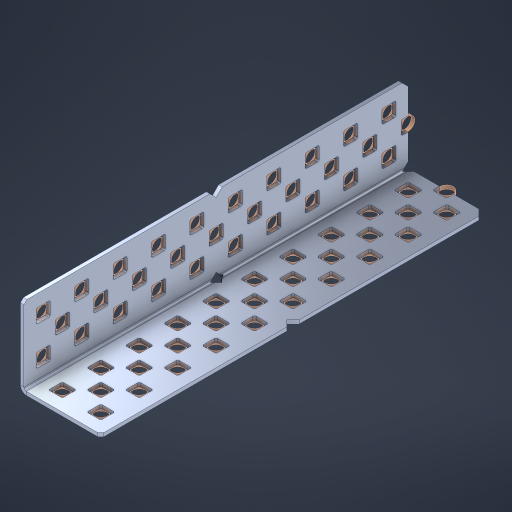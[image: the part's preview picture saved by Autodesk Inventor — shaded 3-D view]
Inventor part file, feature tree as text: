
AUTODESK INVENTOR PART (.ipt)
format: ipt  version: 2023 (Build 270158000, 158)  size: 969,216 bytes
history: native  units: in
note: dims shown in document units (in); Inventor stores cm internally (conversion verified against a paired STEP export)
features: other x66, extrude x58, sheet_metal_op x8, sketch x7, pattern_linear x2, mirror x1, chamfer x1
ambient origin geometry x8: Origin, YZ Plane, XZ Plane, XY Plane, X Axis, Y Axis, Z Axis, Center Point
bodies: Solid1 (feature_tree), Body (feature_tree)
feature tree (143):
  sheet_metal_op  "Flanges"
  sheet_metal_op  "Body Pattern"
  pattern_linear  "Center Pattern"  Spacing1=1.0in  [1 undecoded]
  other  "Arc Length"
  pattern_linear  "Notch Pattern"  Spacing1=0.1875in  [1 undecoded]
  other  "Diagonal Plane"
  mirror  "Everything Mirrored"
  chamfer  "End Chamfer"
  sketch  "Sketch1"  dims[d0=1.0in]
  other  "Plate1"
  sketch  "Sketch2"  dims[d1=5.0in]
  other  "Plate2"
  sheet_metal_op  "Bend1"
  sheet_metal_op  "Corner1"
  sketch  "Sketch8"  dims[d2=0.0469in]
  sketch  "Sketch9"  dims[d3=0.0469in]
  other  "Srf91"
  sheet_metal_op  "Body Pattern Sketch"
  other  "Srf92"
  sketch  "Sketch13"  dims[d4=0.0234in]
  sketch  "Sketch15"  dims[d5=0.0938in]
  sketch  "Sketch16"  dims[d6=0.0469in d7=1.0in d8=90.0deg d9=0.0312in d10=0.1875in d11=0.0469in d12=0.0469in d49=0.182in d50=0.02in d52=0.25in d53=0.0469in d54=0.0in d55=0.172in d56=1.0in d57=0.0in d60=3.937in d62=0.5in d63=0.7874in d65=0.5in d85=0.1473in d86=0.1659in d89=0.0469in d90=0.0in d91=0.04in d92=0.0491in d95=2.5in d96=0.04in d97=0.25in d98=45.0deg d99=0.25in d106=0.182in d107=0.02in d108=0.5in d110=0.0469in d111=0.0in d112=0.172in d113=0.5in d114=0.0in d117=0.5in d123=0.25in d125=0.25in d126=0.0491in d127=0.1227in d128=0.08in d129=0.04in d130=2.5in]
  other  "Srf786"
  other  "Srf856"
  other  "Srf857"
  other  "Srf858"
  other  "Srf859"
  other  "Srf860"
  other  "Srf861"
  other  "Srf889"
  other  "Srf890"
  other  "Srf891"
  other  "Srf1275"
  other  "Srf1276"
  other  "Srf1278"
  other  "Srf1279"
  other  "Srf1280"
  other  "Srf1281"
  other  "Srf1282"
  other  "Srf1283"
  other  "Srf1277"
  other  "Srf1285"
  other  "Srf1286"
  other  "Srf1287"
  other  "Srf1383"
  other  "Srf1384"
  other  "Srf1385"
  other  "Srf1386"
  other  "Srf1387"
  other  "Srf1388"
  other  "Srf1389"
  other  "Srf1390"
  other  "Srf1391"
  other  "Srf1392"
  other  "Srf1393"
  other  "Srf1394"
  other  "Srf1445"
  other  "Srf1446"
  other  "Srf1447"
  other  "Srf1448"
  other  "Srf1449"
  other  "Srf1450"
  other  "Srf1475"
  other  "Srf1476"
  other  "Srf1477"
  other  "Srf1478"
  other  "Srf1479"
  other  "Srf1480"
  other  "Srf1481"
  other  "Srf1482"
  other  "Srf1483"
  other  "Srf1484"
  other  "Srf1485"
  other  "Srf1486"
  other  "Srf1537"
  other  "Srf1538"
  other  "Srf1539"
  other  "Srf1540"
  other  "Srf1541"
  other  "Srf1542"
  sheet_metal_op  "Body Stamp"
  sheet_metal_op  "Body Circle"
  other  "Center Stamp"
  other  "Center Circle"
  sheet_metal_op  "Notch"
  extrude  "ExtrusionSrf92"  Depth=0.0469in
  extrude  "ExtrusionSrf856"  Depth=0.0469in
  extrude  "ExtrusionSrf857"  Depth=2.5in
  extrude  "ExtrusionSrf858"  Depth=0.02in
  extrude  "ExtrusionSrf859"  Depth=2.5in
  extrude  "ExtrusionSrf860"  Depth=0.0469in
  extrude  "ExtrusionSrf861"  TaperAngle=0.0deg  [1 undecoded]
  extrude  "ExtrusionSrf889"  Depth=2.5in
  extrude  "ExtrusionSrf890"  Depth=1.0in TaperAngle=0.0deg
  extrude  "ExtrusionSrf891"  Depth=2.5in
  extrude  "ExtrusionSrf1275"  Depth=0.5in
  extrude  "ExtrusionSrf1276"  Depth=2.5in
  extrude  "ExtrusionSrf1277"  Depth=2.5in
  extrude  "ExtrusionSrf1278"  Depth=0.0469in
  extrude  "ExtrusionSrf1279"  Depth=2.5in TaperAngle=0.0deg
  extrude  "ExtrusionSrf1280"  Depth=2.5in
  extrude  "ExtrusionSrf1281"  Depth=2.5in TaperAngle=45.0deg
  extrude  "ExtrusionSrf1282"  Depth=2.5in
  extrude  "ExtrusionSrf1345"  Depth=2.5in
  extrude  "ExtrusionSrf1346"  Depth=0.02in
  extrude  "ExtrusionSrf1347"  Depth=0.5in
  extrude  "ExtrusionSrf1348"  Depth=0.0469in
  extrude  "ExtrusionSrf1383"  TaperAngle=0.0deg  [1 undecoded]
  extrude  "ExtrusionSrf1384"  Depth=2.5in
  extrude  "ExtrusionSrf1385"  Depth=0.5in TaperAngle=0.0deg
  extrude  "ExtrusionSrf1386"  Depth=0.5in
  extrude  "ExtrusionSrf1387"  Depth=2.5in
  extrude  "ExtrusionSrf1388"  Depth=2.5in
  extrude  "ExtrusionSrf1389"  Depth=2.5in
  extrude  "ExtrusionSrf1390"  Depth=2.5in
  extrude  "ExtrusionSrf1391"  Depth=2.5in
  extrude  "ExtrusionSrf1392"  Depth=2.5in
  extrude  "ExtrusionSrf1393"  Depth=2.5in
  extrude  "ExtrusionSrf1394"  [1 undecoded]
  extrude  "ExtrusionSrf1445"  [1 undecoded]
  extrude  "ExtrusionSrf1446"  [1 undecoded]
  extrude  "ExtrusionSrf1447"  [1 undecoded]
  extrude  "ExtrusionSrf1448"  [1 undecoded]
  extrude  "ExtrusionSrf1449"  [1 undecoded]
  extrude  "ExtrusionSrf1450"  [1 undecoded]
  extrude  "ExtrusionSrf1475"  [1 undecoded]
  extrude  "ExtrusionSrf1476"  [1 undecoded]
  extrude  "ExtrusionSrf1477"  [1 undecoded]
  extrude  "ExtrusionSrf1478"  [1 undecoded]
  extrude  "ExtrusionSrf1479"  [1 undecoded]
  extrude  "ExtrusionSrf1480"  [1 undecoded]
  extrude  "ExtrusionSrf1481"  [1 undecoded]
  extrude  "ExtrusionSrf1482"  [1 undecoded]
  extrude  "ExtrusionSrf1483"  [1 undecoded]
  extrude  "ExtrusionSrf1484"  [1 undecoded]
  extrude  "ExtrusionSrf1485"  [1 undecoded]
  extrude  "ExtrusionSrf1486"  [1 undecoded]
  extrude  "ExtrusionSrf1537"  [1 undecoded]
  extrude  "ExtrusionSrf1538"  [1 undecoded]
  extrude  "ExtrusionSrf1539"  [1 undecoded]
  extrude  "ExtrusionSrf1540"  [1 undecoded]
  extrude  "ExtrusionSrf1541"  [1 undecoded]
  extrude  "ExtrusionSrf1542"  [1 undecoded]
note: 29 required parameter values undecoded (feature->parameter linkage not recoverable at this tier; creation-order binding heuristic only, values carry confidence <= 0.55)
